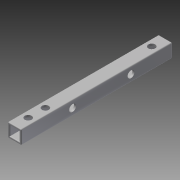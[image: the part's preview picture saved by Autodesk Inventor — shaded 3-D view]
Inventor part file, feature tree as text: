
AUTODESK INVENTOR PART (.ipt)
format: ipt  version: 2013 (Build 170138000, 138)  size: 162,304 bytes
history: native  units: in
note: dims shown in document units (in); Inventor stores cm internally (conversion verified against a paired STEP export)
features: sketch x6, extrude x5, fillet x1
ambient origin geometry x8: Origin, YZ Plane, XZ Plane, XY Plane, X Axis, Y Axis, Z Axis, Center Point
bodies: Solid1 (feature_tree)
feature tree (12):
  extrude  "Extrusion1"  Depth=1.0in
  extrude  "Extrusion2"  Depth=1.0in
  extrude  "Extrusion3"  Depth=1.0in
  extrude  "Extrusion4"  Depth=11.0in TaperAngle=0.0deg
  sketch  "Sketch5"  dims[d10=0.15in d11=0.15in d12=0.15in]
  extrude  "Extrusion5"  Depth=0.15in
  fillet  "Fillet1"  Radius=0.15in
  sketch  "Sketch1"  dims[d0=1.0in d1=1.0in]
  sketch  "Sketch2"  dims[d2=11.0in d3=0.0in d4=1.0in]
  sketch  "Sketch3"  dims[d5=0.5in d6=1.0in]
  sketch  "Sketch4"  dims[d7=0.5in d8=11.0in d9=0.0in]
  sketch  "Sketch6"  dims[d13=0.15in d14=0.15in d15=0.15in d16=0.15in d17=0.15in d18=11.0in d19=0.0in d20=1.0in d21=0.5in d22=11.0in d23=0.0in d24=1.5in d25=0.5in d26=4.0in d27=0.5in d28=11.0in d29=0.0in d30=0.0625in]
